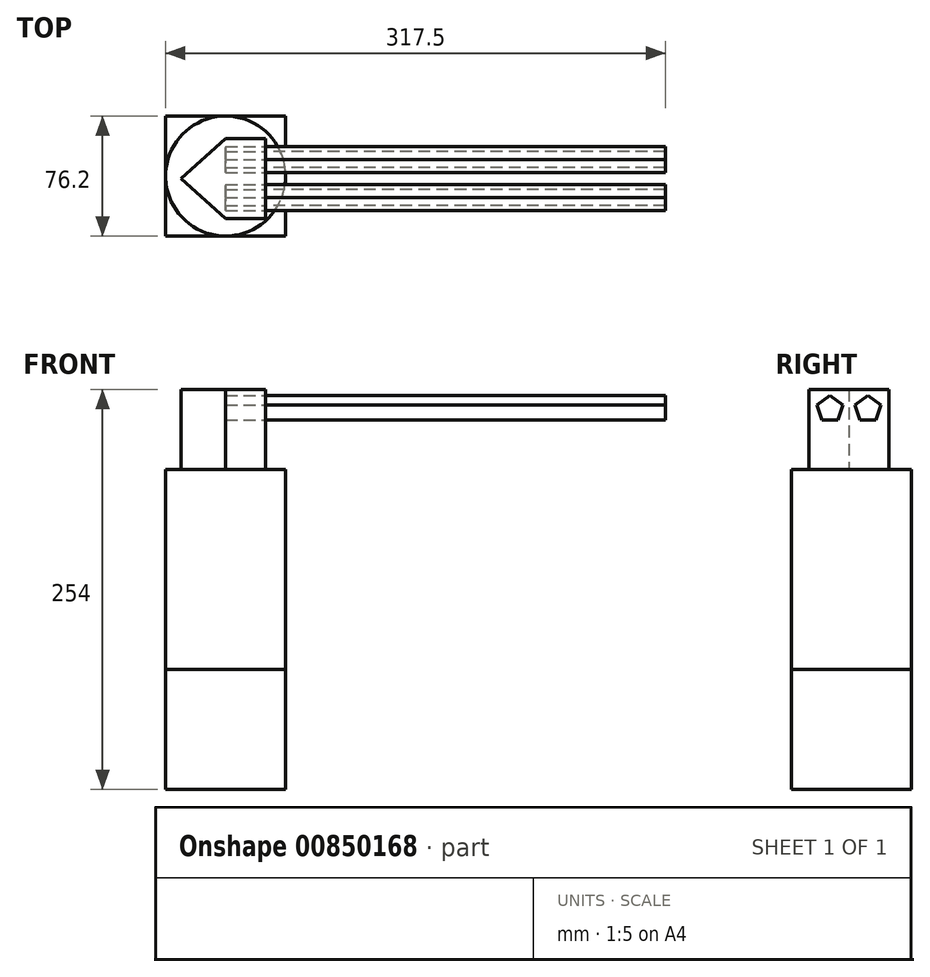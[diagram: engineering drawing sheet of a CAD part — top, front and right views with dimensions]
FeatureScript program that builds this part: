
annotation { "Feature Type Name" : "Feature", "Feature Type Description" : "" }
export const myFeature = defineFeature(function(context is Context, id is Id, definition is map)
    precondition{}
    {
        {
            var Q0;
            Q0=qCreatedBy(makeId("Top.planeOp"),FACE);
            var sketch = newSketch(context, id + "F0", { "sketchPlane" : qUnion([Q0])});
            skLineSegment(sketch, "E0.bottom", {"start": v(38.1, -38.1) * mm, "end": v(-38.1, -38.1) * mm});
            skLineSegment(sketch, "E0.top", {"start": v(38.1, 38.1) * mm, "end": v(-38.1, 38.1) * mm});
            skLineSegment(sketch, "E0.left", {"start": v(38.1, -38.1) * mm, "end": v(38.1, 38.1) * mm});
            skLineSegment(sketch, "E0.right", {"start": v(-38.1, -38.1) * mm, "end": v(-38.1, 38.1) * mm});
            skPoint(sketch, "E0.middle", {"position": v(0, 0) * mm});
            skSolve(sketch);
        }
        {
            var Q0;
            Q0=makeQuery(id+"F0.imprint","IMPRINT",FACE,{"disambiguationData":[TD([[makeQuery(id+"F0.imprint","IMPRINT",EDGE,{"derivedFrom":sQuery(id+"F0.wireOp",EDGE,"E0.bottom")}),-1.0]])]});
            extrude(context, id + "F1", {"entities" : qUnion([Q0]), "depth" : 76.2 * mm, "offsetDistance" : 25.4 * mm});
        }
        {
            var Q0;
            Q0=makeQuery(id+"F1.opExtrude","CAP_FACE",FACE,{"disambiguationData":[OSD([sQuery(id+"F0.wireOp",EDGE,"E0.bottom"),sQuery(id+"F0.wireOp",EDGE,"E0.top"),sQuery(id+"F0.wireOp",EDGE,"E0.left"),sQuery(id+"F0.wireOp",EDGE,"E0.right")])],"isStart":false});
            var sketch = newSketch(context, id + "F2", { "sketchPlane" : qUnion([Q0])});
            skCircle(sketch, "E1", {"center": v(0, 0) * mm, "radius": 38.1 * mm});
            skSolve(sketch);
        }
        {
            var Q0;
            Q0 = qSketchRegion(id + "F2", true);
            extrude(context, id + "F3", {"entities" : qUnion([Q0]), "operationType" : NewBodyOperationType.ADD, "depth" : 127 * mm, "offsetDistance" : 25.4 * mm});
        }
        {
            var Q0;
            Q0=makeQuery(id+"F3.opExtrude","CAP_FACE",FACE,{"disambiguationData":[OSD([sQuery(id+"F2.wireOp",EDGE,"E1")])],"isStart":false});
            var sketch = newSketch(context, id + "F4", { "sketchPlane" : qUnion([Q0])});
            skLineSegment(sketch, "E2", {"start": v(0, 23.89) * mm, "end": v(25.4, 23.89) * mm});
            skLineSegment(sketch, "E3", {"start": v(25.4, 23.89) * mm, "end": v(25.4, -26.91) * mm});
            skLineSegment(sketch, "E4", {"start": v(25.4, -26.91) * mm, "end": v(0, -26.91) * mm});
            skLineSegment(sketch, "E5", {"start": v(0, -26.91) * mm, "end": v(-28.4, -1.51) * mm});
            skLineSegment(sketch, "E6", {"start": v(-28.4, -1.51) * mm, "end": v(0, 23.89) * mm});
            skSolve(sketch);
        }
        {
            var Q0;
            Q0=makeQuery(id+"F4.imprint","IMPRINT",FACE,{"disambiguationData":[TD([[makeQuery(id+"F4.imprint","IMPRINT",EDGE,{"derivedFrom":sQuery(id+"F4.wireOp",EDGE,"E2")}),-1.0]])]});
            extrude(context, id + "F5", {"entities" : qUnion([Q0]), "depth" : 50.8 * mm, "offsetDistance" : 25.4 * mm});
        }
        {
            var Q0;
            Q0=makeQuery(id+"F5.opExtrude","SWEPT_FACE",FACE,{"disambiguationData":[OSD([sQuery(id+"F4.wireOp",EDGE,"E3")])]});
            var sketch = newSketch(context, id + "F6", { "sketchPlane" : qUnion([Q0])});
            skCircle(sketch, "E7.cCircle", {"center": v(-13.61, 241.55) * mm, "radius": 7 * mm, "construction": true});
            skLineSegment(sketch, "E7.0", {"start": v(-8.53, 234.56) * mm, "end": v(-18.7, 234.56) * mm});
            skLineSegment(sketch, "E7.1", {"start": v(-18.7, 234.56) * mm, "end": v(-21.83, 244.22) * mm});
            skLineSegment(sketch, "E7.2", {"start": v(-21.83, 244.22) * mm, "end": v(-13.61, 250.2) * mm});
            skLineSegment(sketch, "E7.3", {"start": v(-13.61, 250.19) * mm, "end": v(-5.4, 244.22) * mm});
            skLineSegment(sketch, "E7.4", {"start": v(-5.4, 244.22) * mm, "end": v(-8.53, 234.56) * mm});
            skPoint(sketch, "E7.0.midPoint", {"position": v(-13.61, 234.56) * mm});
            skCircle(sketch, "E8.cCircle", {"center": v(10.59, 241.55) * mm, "radius": 7 * mm, "construction": true});
            skLineSegment(sketch, "E8.0", {"start": v(15.67, 234.56) * mm, "end": v(5.5, 234.56) * mm});
            skLineSegment(sketch, "E8.1", {"start": v(5.5, 234.56) * mm, "end": v(2.37, 244.22) * mm});
            skLineSegment(sketch, "E8.2", {"start": v(2.37, 244.22) * mm, "end": v(10.59, 250.2) * mm});
            skLineSegment(sketch, "E8.3", {"start": v(10.59, 250.2) * mm, "end": v(18.8, 244.22) * mm});
            skLineSegment(sketch, "E8.4", {"start": v(18.8, 244.22) * mm, "end": v(15.67, 234.56) * mm});
            skPoint(sketch, "E8.0.midPoint", {"position": v(10.59, 234.56) * mm});
            skSolve(sketch);
        }
        {
            var Q0;
            Q0=makeQuery(id+"F6.imprint","IMPRINT",FACE,{"disambiguationData":[TD([[makeQuery(id+"F6.imprint","IMPRINT",EDGE,{"derivedFrom":sQuery(id+"F6.wireOp",EDGE,"E7.0")}),-1.0]])]});
            var Q1;
            Q1=makeQuery(id+"F6.imprint","IMPRINT",FACE,{"disambiguationData":[TD([[makeQuery(id+"F6.imprint","IMPRINT",EDGE,{"derivedFrom":sQuery(id+"F6.wireOp",EDGE,"E8.0")}),-1.0]])]});
            extrude(context, id + "F7", {"entities" : qUnion([Q0, Q1]), "operationType" : NewBodyOperationType.REMOVE, "oppositeDirection" : true, "depth" : 25.4 * mm, "offsetDistance" : 25.4 * mm});
        }
        {
            var Q0;
            Q0 = qSketchRegion(id + "F6", true);
            extrude(context, id + "F8", {"entities" : qUnion([Q0]), "depth" : 254 * mm, "offsetDistance" : 25.4 * mm});
        }
    });
